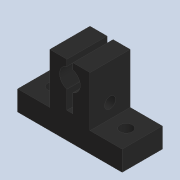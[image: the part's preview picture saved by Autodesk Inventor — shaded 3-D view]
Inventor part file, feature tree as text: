
AUTODESK INVENTOR PART (.ipt)
format: ipt  version: 2020 (Build 240168000, 168)  size: 161,792 bytes
history: native  units: mm
features: sketch x3, extrude x2, hole x1
ambient origin geometry x8: Origin, YZ Plane, XZ Plane, XY Plane, X Axis, Y Axis, Z Axis, Center Point
bodies: Solid1 (feature_tree)
feature tree (6):
  extrude  "Extrusion1"  Depth=20.0mm
  hole  "Hole1"  [1 undecoded]
  extrude  "Extrusion2"  Depth=3.0mm
  sketch  "Sketch1"  dims[d0=10.0mm d1=20.0mm]
  sketch  "Sketch2"  dims[d2=10.3mm d3=17.0mm]
  sketch  "Sketch3"  dims[d4=8.0mm d5=3.0mm d6=14.0mm d7=18.0mm d8=20.0mm d9=0.0mm d10=6.0mm d11=6.0mm d12=11.0mm d13=2.0mm d14=90.0deg d15=8.0mm d16=20.594885mm d18=5.5mm d19=8.0mm d21=8.0mm d22=13.0mm d23=0.0mm d24=5.0mm d25=8.0mm d26=8.0mm]
note: 1 required parameter value undecoded (feature->parameter linkage not recoverable at this tier; creation-order binding heuristic only, values carry confidence <= 0.55)
